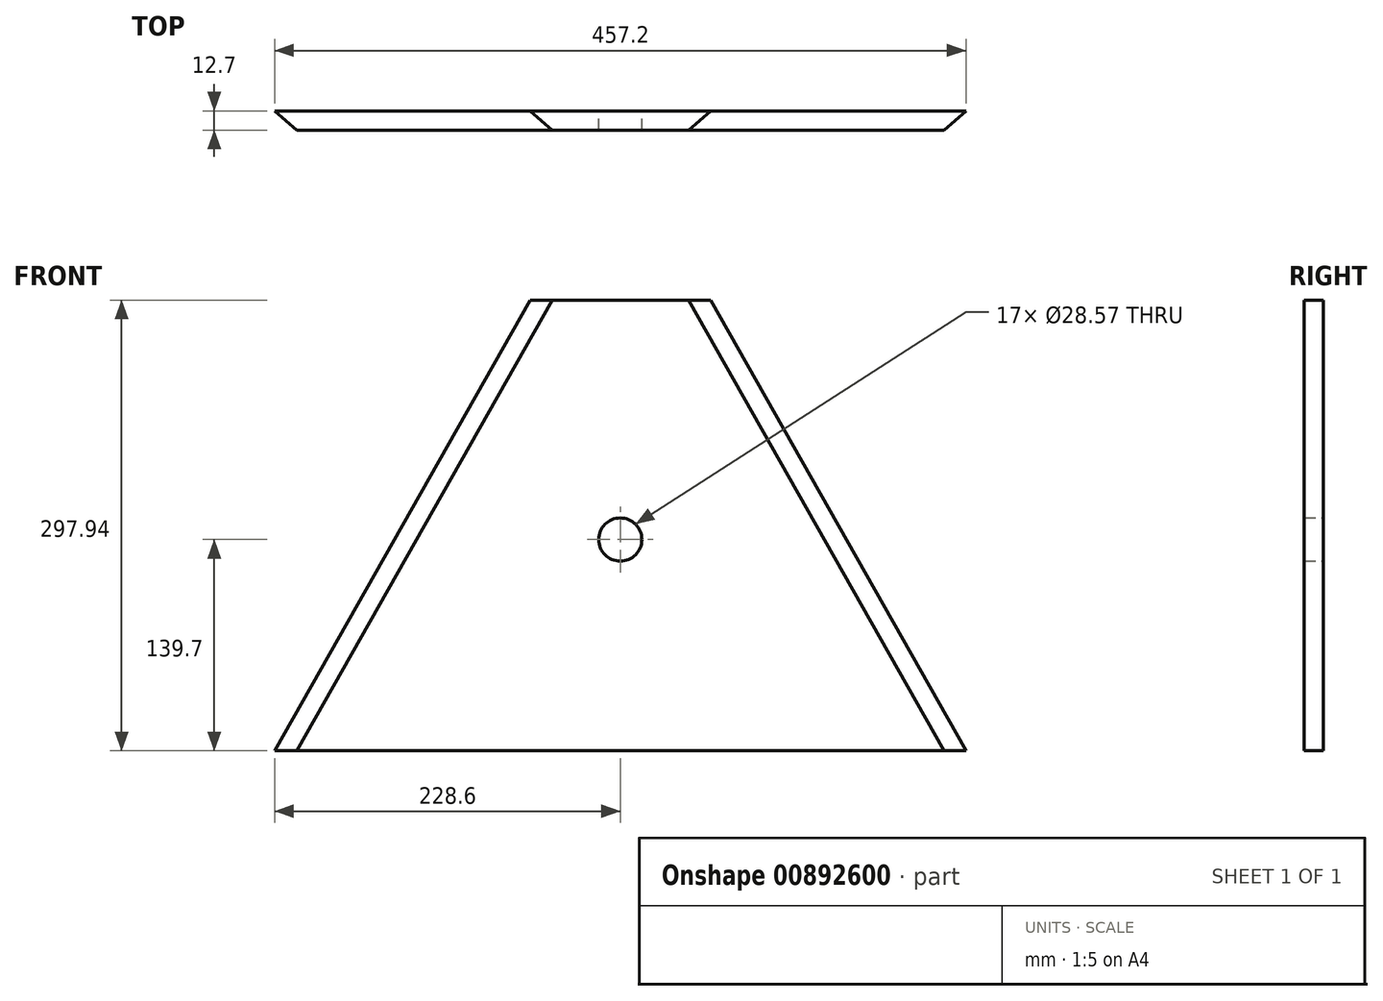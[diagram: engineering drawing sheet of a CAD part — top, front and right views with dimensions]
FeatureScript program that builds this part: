
annotation { "Feature Type Name" : "Feature", "Feature Type Description" : "" }
export const myFeature = defineFeature(function(context is Context, id is Id, definition is map)
    precondition{}
    {
        {
            var Q0;
            Q0=qCreatedBy(makeId("Front.planeOp"),FACE);
            var sketch = newSketch(context, id + "F0", { "sketchPlane" : qUnion([Q0])});
            skLineSegment(sketch, "E0", {"start": v(228.6, 0) * mm, "end": v(-228.6, 0) * mm});
            skLineSegment(sketch, "E1", {"start": v(-228.6, 0) * mm, "end": v(-59.68, 297.94) * mm});
            skLineSegment(sketch, "E2", {"start": v(-59.68, 297.94) * mm, "end": v(59.68, 297.94) * mm});
            skLineSegment(sketch, "E3", {"start": v(59.68, 297.94) * mm, "end": v(228.6, 0) * mm});
            skCircle(sketch, "E4", {"center": v(0, 139.7) * mm, "radius": 14.29 * mm});
            skSolve(sketch);
        }
        {
            var Q0;
            Q0=makeQuery(id+"F0.imprint","IMPRINT",FACE,{"disambiguationData":[TD([[makeQuery(id+"F0.imprint","IMPRINT",EDGE,{"derivedFrom":sQuery(id+"F0.wireOp",EDGE,"E0")}),-1.0]])]});
            extrude(context, id + "F1", {"entities" : qUnion([Q0]), "depth" : 12.7 * mm, "offsetDistance" : 25.4 * mm});
        }
        {
            var Q0;
            Q0=makeQuery(id+"F1.opExtrude","CAP_EDGE",EDGE,{"disambiguationData":[OSD([sQuery(id+"F0.wireOp",EDGE,"E3")])],"isStart":false});
            chamfer(context, id + "F2", {"entities" : qUnion([Q0]), "chamferType" : ChamferType.OFFSET_ANGLE, "width" : 12.7 * mm, "oppositeDirection" : false, "angle" : 45 * degree, "tangentPropagation" : true});
        }
        {
            var Q0;
            Q0=makeQuery(id+"F1.opExtrude","CAP_EDGE",EDGE,{"disambiguationData":[OSD([sQuery(id+"F0.wireOp",EDGE,"E1")])],"isStart":false});
            chamfer(context, id + "F3", {"entities" : qUnion([Q0]), "chamferType" : ChamferType.OFFSET_ANGLE, "width" : 12.7 * mm, "oppositeDirection" : false, "angle" : 45 * degree, "tangentPropagation" : true});
        }
    });
